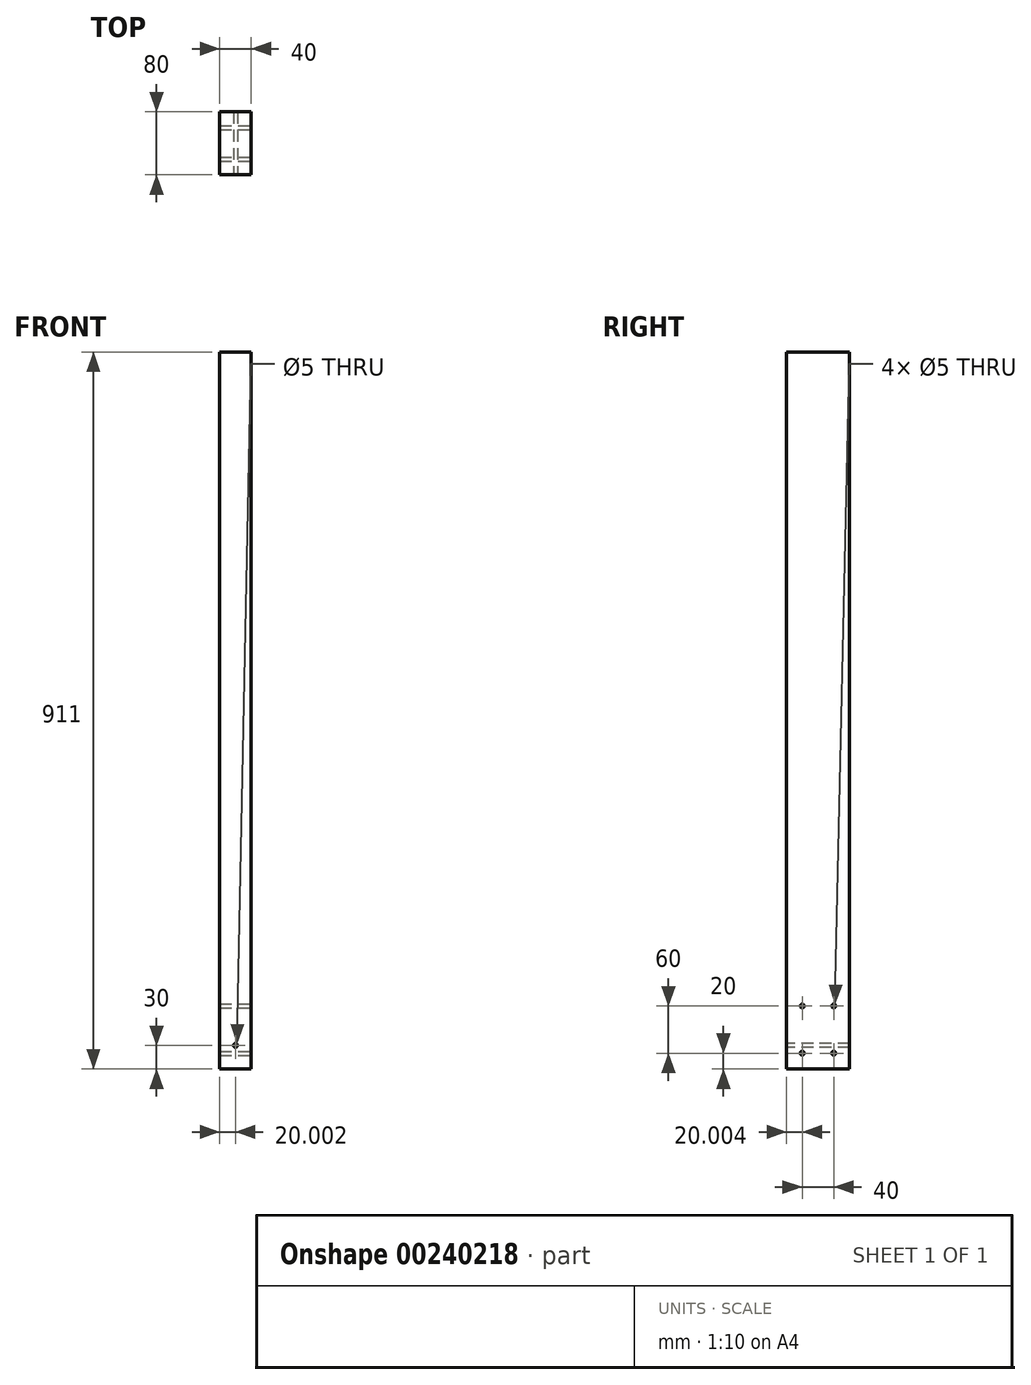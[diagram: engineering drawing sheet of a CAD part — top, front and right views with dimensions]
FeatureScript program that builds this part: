
annotation { "Feature Type Name" : "Feature", "Feature Type Description" : "" }
export const myFeature = defineFeature(function(context is Context, id is Id, definition is map)
    precondition{}
    {
        {
            var Q0;
            Q0=qCreatedBy(makeId("Top.planeOp"),FACE);
            var sketch = newSketch(context, id + "F0", { "sketchPlane" : qUnion([Q0])});
            skLineSegment(sketch, "E0.bottom", {"start": v(-20.59, 34.44) * mm, "end": v(19.41, 34.44) * mm});
            skLineSegment(sketch, "E0.top", {"start": v(-20.59, -45.56) * mm, "end": v(19.41, -45.56) * mm});
            skLineSegment(sketch, "E0.left", {"start": v(-20.59, 34.44) * mm, "end": v(-20.59, -45.56) * mm});
            skLineSegment(sketch, "E0.right", {"start": v(19.41, 34.44) * mm, "end": v(19.41, -45.56) * mm});
            skSolve(sketch);
        }
        {
            var Q0;
            Q0 = qSketchRegion(id + "F0", true);
            extrude(context, id + "F1", {"entities" : qUnion([Q0]), "depth" : 821 * mm + 80 * mm + 10 * mm});
        }
        {
            var Q0;
            Q0=makeQuery(id+"F1.opExtrude","SWEPT_FACE",FACE,{"disambiguationData":[OSD([sQuery(id+"F0.wireOp",EDGE,"E0.right")])]});
            var sketch = newSketch(context, id + "F2", { "sketchPlane" : qUnion([Q0])});
            skLineSegment(sketch, "E1.bottom", {"start": v(-25.56, 80) * mm, "end": v(14.44, 80) * mm, "construction": true});
            skLineSegment(sketch, "E1.top", {"start": v(-25.56, 20) * mm, "end": v(14.44, 20) * mm, "construction": true});
            skLineSegment(sketch, "E1.left", {"start": v(-25.56, 80) * mm, "end": v(-25.56, 20) * mm, "construction": true});
            skLineSegment(sketch, "E1.right", {"start": v(14.44, 80) * mm, "end": v(14.44, 20) * mm, "construction": true});
            skLineSegment(sketch, "E2", {"start": v(-25.56, 20) * mm, "end": v(-45.56, 20) * mm, "construction": true});
            skLineSegment(sketch, "E3", {"start": v(-25.56, 20) * mm, "end": v(-25.56, 0) * mm, "construction": true});
            skCircle(sketch, "E4", {"center": v(-25.56, 80) * mm, "radius": 2.5 * mm});
            skCircle(sketch, "E5", {"center": v(14.44, 80) * mm, "radius": 2.5 * mm});
            skCircle(sketch, "E6", {"center": v(14.44, 20) * mm, "radius": 2.5 * mm});
            skCircle(sketch, "E7", {"center": v(-25.56, 20) * mm, "radius": 2.5 * mm});
            skSolve(sketch);
        }
        {
            var Q0;
            Q0 = qSketchRegion(id + "F2", true);
            extrude(context, id + "F3", {"entities" : qUnion([Q0]), "operationType" : NewBodyOperationType.REMOVE, "endBound" : BoundingType.THROUGH_ALL, "oppositeDirection" : true, "depth" : 25 * mm});
        }
        {
            var Q0;
            Q0=makeQuery(id+"F1.opExtrude","SWEPT_FACE",FACE,{"disambiguationData":[OSD([sQuery(id+"F0.wireOp",EDGE,"E0.top")])]});
            var sketch = newSketch(context, id + "F4", { "sketchPlane" : qUnion([Q0])});
            skLineSegment(sketch, "E8", {"start": v(-20.59, 30) * mm, "end": v(-0.59, 30) * mm, "construction": true});
            skLineSegment(sketch, "E9", {"start": v(-0.59, 30) * mm, "end": v(19.41, 30) * mm, "construction": true});
            skCircle(sketch, "E10", {"center": v(-0.59, 30) * mm, "radius": 2.5 * mm});
            skSolve(sketch);
        }
        {
            var Q0;
            Q0 = qSketchRegion(id + "F4", true);
            extrude(context, id + "F5", {"entities" : qUnion([Q0]), "operationType" : NewBodyOperationType.REMOVE, "endBound" : BoundingType.THROUGH_ALL, "oppositeDirection" : true, "depth" : 25 * mm});
        }
    });
